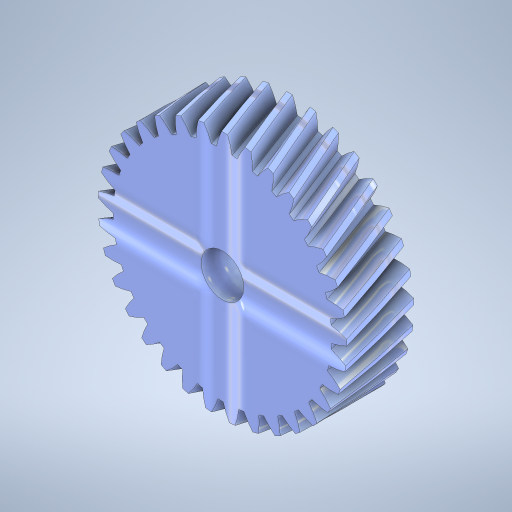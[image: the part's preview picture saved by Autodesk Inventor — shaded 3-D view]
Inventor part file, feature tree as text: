
AUTODESK INVENTOR PART (.ipt)
format: ipt  version: 2024 (Build 280153000, 153)  size: 796,672 bytes
history: native  units: mm (DEFAULTED — no unit token found)
features: plane x3, other x3, extrude x2, sketch x1
ambient origin geometry x8: Origin, YZ Plane, XZ Plane, XY Plane, X Axis, Y Axis, Z Axis, Center Point
bodies: Solid1 (feature_tree)
feature tree (9):
  extrude  "Extrusion1"  Depth=15.0mm TaperAngle=0.0deg
  plane  "Work Plane2"
  plane  "Work Plane8"
  plane  "Work Plane9"
  other  "Spur Gear"
  extrude  "Extrusion2"  Depth=10.0mm
  sketch  "Sketch1"  dims[d0=55.6768mm d1=15.0mm d2=0.0mm d3=52.6768mm d4=10.0mm d5=0.0mm d16=63.909111mm d17=0.0mm d34=0.951998mm d39=0.0mm d41=0.0mm d43=63.909111mm d46=63.909111mm d47=0.0mm d48=0.0mm d49=9.525mm d50=0.0mm d51=0.0mm]
  other  "Srf1"
  other  "Pitch Diameter"
